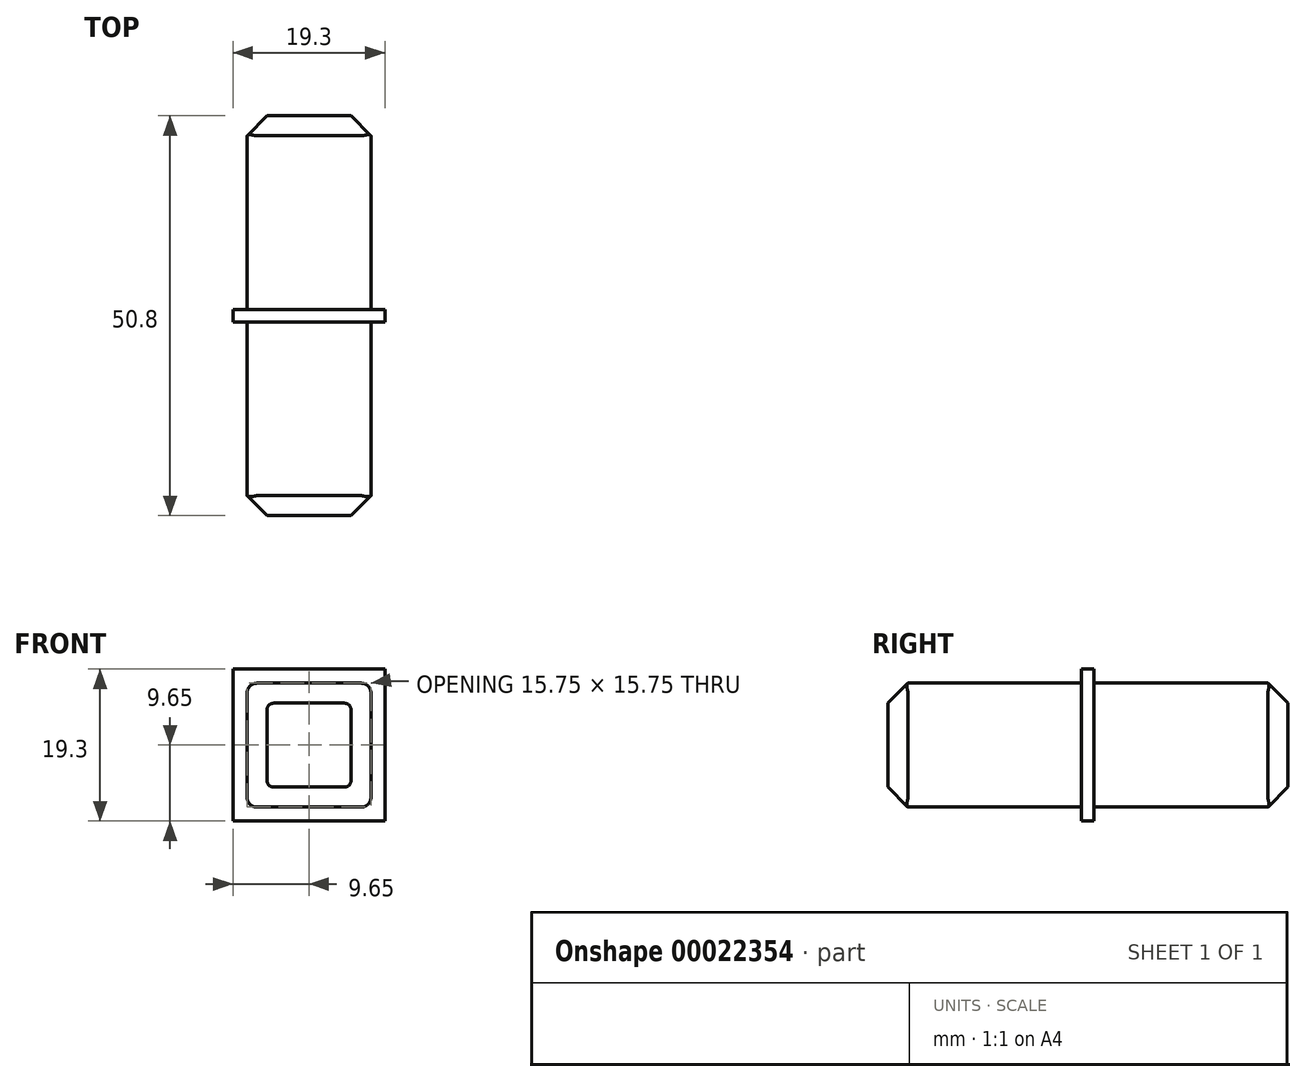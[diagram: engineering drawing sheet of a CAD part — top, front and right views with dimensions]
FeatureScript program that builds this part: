
annotation { "Feature Type Name" : "Feature", "Feature Type Description" : "" }
export const myFeature = defineFeature(function(context is Context, id is Id, definition is map)
    precondition{}
    {
        {
            var Q0;
            Q0=qCreatedBy(makeId("Front.planeOp"),FACE);
            var sketch = newSketch(context, id + "F0", { "sketchPlane" : qUnion([Q0])});
            skLineSegment(sketch, "E0.rect.bottom", {"start": v(9.65, 9.65) * mm, "end": v(-9.65, 9.65) * mm});
            skLineSegment(sketch, "E0.rect.top", {"start": v(9.65, -9.65) * mm, "end": v(-9.65, -9.65) * mm});
            skLineSegment(sketch, "E0.rect.left", {"start": v(9.65, 9.65) * mm, "end": v(9.65, -9.65) * mm});
            skLineSegment(sketch, "E0.rect.right", {"start": v(-9.65, 9.65) * mm, "end": v(-9.65, -9.65) * mm});
            skPoint(sketch, "E0.rect.middle", {"position": v(0, 0) * mm});
            skSolve(sketch);
        }
        {
            var Q0;
            Q0 = qSketchRegion(id + "F0", true);
            extrude(context, id + "F1", {"entities" : qUnion([Q0]), "endBound" : BoundingType.SYMMETRIC, "depth" : 1.59 * mm});
        }
        {
            var Q0;
            Q0=qCreatedBy(makeId("Front.planeOp"),FACE);
            var sketch = newSketch(context, id + "F2", { "sketchPlane" : qUnion([Q0])});
            skLineSegment(sketch, "E1.rect.bottom", {"start": v(7.87, 7.87) * mm, "end": v(-7.87, 7.87) * mm});
            skLineSegment(sketch, "E1.rect.top", {"start": v(7.87, -7.87) * mm, "end": v(-7.87, -7.87) * mm});
            skLineSegment(sketch, "E1.rect.left", {"start": v(7.87, 7.87) * mm, "end": v(7.87, -7.87) * mm});
            skLineSegment(sketch, "E1.rect.right", {"start": v(-7.87, 7.87) * mm, "end": v(-7.87, -7.87) * mm});
            skPoint(sketch, "E1.rect.middle", {"position": v(0, 0) * mm});
            skSolve(sketch);
        }
        {
            var Q0;
            Q0 = qSketchRegion(id + "F2", true);
            extrude(context, id + "F3", {"entities" : qUnion([Q0]), "operationType" : NewBodyOperationType.ADD, "endBound" : BoundingType.SYMMETRIC, "depth" : 50.8 * mm});
        }
        {
            var Q0;
            Q0=makeQuery(id+"F3.opExtrude","CAP_FACE",FACE,{"disambiguationData":[OSD([sQuery(id+"F2.wireOp",EDGE,"E1.rect.bottom"),sQuery(id+"F2.wireOp",EDGE,"E1.rect.top"),sQuery(id+"F2.wireOp",EDGE,"E1.rect.left"),sQuery(id+"F2.wireOp",EDGE,"E1.rect.right")])],"isStart":false});
            var Q1;
            Q1=makeQuery(id+"F3.opExtrude","CAP_FACE",FACE,{"disambiguationData":[OSD([sQuery(id+"F2.wireOp",EDGE,"E1.rect.bottom"),sQuery(id+"F2.wireOp",EDGE,"E1.rect.top"),sQuery(id+"F2.wireOp",EDGE,"E1.rect.left"),sQuery(id+"F2.wireOp",EDGE,"E1.rect.right")])],"isStart":true});
            chamfer(context, id + "F4", {"entities" : qUnion([Q0, Q1]), "width" : 2.54 * mm, "tangentPropagation" : true});
        }
        {
            var Q0;
            {var subQ0=sQuery(id+"F2.wireOp",EDGE,"E1.rect.bottom");var subQ1=sQuery(id+"F2.wireOp",EDGE,"E1.rect.left");Q0=makeQuery(id+"F3.boolean.opBoolean","SPLIT",EDGE,{"disambiguationData":[TD([makeQuery(id+"F1.opExtrude","CAP_FACE",FACE,{"disambiguationData":[OSD([sQuery(id+"F0.wireOp",EDGE,"E0.rect.bottom"),sQuery(id+"F0.wireOp",EDGE,"E0.rect.top"),sQuery(id+"F0.wireOp",EDGE,"E0.rect.left"),sQuery(id+"F0.wireOp",EDGE,"E0.rect.right")])],"isStart":false})])],"derivedFrom":makeQuery(id+"F3.opExtrude","SWEPT_EDGE",EDGE,{"disambiguationData":[OSD([subQ0,subQ1])]})});}
            var Q1;
            {var subQ0=sQuery(id+"F2.wireOp",EDGE,"E1.rect.bottom");var subQ1=sQuery(id+"F2.wireOp",EDGE,"E1.rect.right");Q1=makeQuery(id+"F3.boolean.opBoolean","SPLIT",EDGE,{"disambiguationData":[TD([makeQuery(id+"F1.opExtrude","CAP_FACE",FACE,{"disambiguationData":[OSD([sQuery(id+"F0.wireOp",EDGE,"E0.rect.bottom"),sQuery(id+"F0.wireOp",EDGE,"E0.rect.top"),sQuery(id+"F0.wireOp",EDGE,"E0.rect.left"),sQuery(id+"F0.wireOp",EDGE,"E0.rect.right")])],"isStart":false})])],"derivedFrom":makeQuery(id+"F3.opExtrude","SWEPT_EDGE",EDGE,{"disambiguationData":[OSD([subQ0,subQ1])]})});}
            var Q2;
            {var subQ0=sQuery(id+"F2.wireOp",EDGE,"E1.rect.bottom");var subQ1=sQuery(id+"F2.wireOp",EDGE,"E1.rect.left");Q2=makeQuery(id+"F3.boolean.opBoolean","SPLIT",EDGE,{"disambiguationData":[TD([makeQuery(id+"F1.opExtrude","CAP_FACE",FACE,{"disambiguationData":[OSD([sQuery(id+"F0.wireOp",EDGE,"E0.rect.bottom"),sQuery(id+"F0.wireOp",EDGE,"E0.rect.top"),sQuery(id+"F0.wireOp",EDGE,"E0.rect.left"),sQuery(id+"F0.wireOp",EDGE,"E0.rect.right")])],"isStart":true})])],"derivedFrom":makeQuery(id+"F3.opExtrude","SWEPT_EDGE",EDGE,{"disambiguationData":[OSD([subQ0,subQ1])]})});}
            var Q3;
            {var subQ0=sQuery(id+"F2.wireOp",EDGE,"E1.rect.bottom");var subQ1=sQuery(id+"F2.wireOp",EDGE,"E1.rect.right");Q3=makeQuery(id+"F3.boolean.opBoolean","SPLIT",EDGE,{"disambiguationData":[TD([makeQuery(id+"F1.opExtrude","CAP_FACE",FACE,{"disambiguationData":[OSD([sQuery(id+"F0.wireOp",EDGE,"E0.rect.bottom"),sQuery(id+"F0.wireOp",EDGE,"E0.rect.top"),sQuery(id+"F0.wireOp",EDGE,"E0.rect.left"),sQuery(id+"F0.wireOp",EDGE,"E0.rect.right")])],"isStart":true})])],"derivedFrom":makeQuery(id+"F3.opExtrude","SWEPT_EDGE",EDGE,{"disambiguationData":[OSD([subQ0,subQ1])]})});}
            var Q4;
            {var subQ0=sQuery(id+"F2.wireOp",EDGE,"E1.rect.top");var subQ1=sQuery(id+"F2.wireOp",EDGE,"E1.rect.left");Q4=makeQuery(id+"F3.boolean.opBoolean","SPLIT",EDGE,{"disambiguationData":[TD([makeQuery(id+"F1.opExtrude","CAP_FACE",FACE,{"disambiguationData":[OSD([sQuery(id+"F0.wireOp",EDGE,"E0.rect.bottom"),sQuery(id+"F0.wireOp",EDGE,"E0.rect.top"),sQuery(id+"F0.wireOp",EDGE,"E0.rect.left"),sQuery(id+"F0.wireOp",EDGE,"E0.rect.right")])],"isStart":true})])],"derivedFrom":makeQuery(id+"F3.opExtrude","SWEPT_EDGE",EDGE,{"disambiguationData":[OSD([subQ0,subQ1])]})});}
            var Q5;
            {var subQ0=sQuery(id+"F2.wireOp",EDGE,"E1.rect.top");var subQ1=sQuery(id+"F2.wireOp",EDGE,"E1.rect.right");Q5=makeQuery(id+"F3.boolean.opBoolean","SPLIT",EDGE,{"disambiguationData":[TD([makeQuery(id+"F1.opExtrude","CAP_FACE",FACE,{"disambiguationData":[OSD([sQuery(id+"F0.wireOp",EDGE,"E0.rect.bottom"),sQuery(id+"F0.wireOp",EDGE,"E0.rect.top"),sQuery(id+"F0.wireOp",EDGE,"E0.rect.left"),sQuery(id+"F0.wireOp",EDGE,"E0.rect.right")])],"isStart":true})])],"derivedFrom":makeQuery(id+"F3.opExtrude","SWEPT_EDGE",EDGE,{"disambiguationData":[OSD([subQ0,subQ1])]})});}
            var Q6;
            {var subQ0=sQuery(id+"F2.wireOp",EDGE,"E1.rect.top");var subQ1=sQuery(id+"F2.wireOp",EDGE,"E1.rect.left");Q6=makeQuery(id+"F3.boolean.opBoolean","SPLIT",EDGE,{"disambiguationData":[TD([makeQuery(id+"F1.opExtrude","CAP_FACE",FACE,{"disambiguationData":[OSD([sQuery(id+"F0.wireOp",EDGE,"E0.rect.bottom"),sQuery(id+"F0.wireOp",EDGE,"E0.rect.top"),sQuery(id+"F0.wireOp",EDGE,"E0.rect.left"),sQuery(id+"F0.wireOp",EDGE,"E0.rect.right")])],"isStart":false})])],"derivedFrom":makeQuery(id+"F3.opExtrude","SWEPT_EDGE",EDGE,{"disambiguationData":[OSD([subQ0,subQ1])]})});}
            var Q7;
            {var subQ0=sQuery(id+"F2.wireOp",EDGE,"E1.rect.top");var subQ1=sQuery(id+"F2.wireOp",EDGE,"E1.rect.right");Q7=makeQuery(id+"F3.boolean.opBoolean","SPLIT",EDGE,{"disambiguationData":[TD([makeQuery(id+"F1.opExtrude","CAP_FACE",FACE,{"disambiguationData":[OSD([sQuery(id+"F0.wireOp",EDGE,"E0.rect.bottom"),sQuery(id+"F0.wireOp",EDGE,"E0.rect.top"),sQuery(id+"F0.wireOp",EDGE,"E0.rect.left"),sQuery(id+"F0.wireOp",EDGE,"E0.rect.right")])],"isStart":false})])],"derivedFrom":makeQuery(id+"F3.opExtrude","SWEPT_EDGE",EDGE,{"disambiguationData":[OSD([subQ0,subQ1])]})});}
            var Q8;
            Q8=makeQuery(id+"F4.opChamfer","BLEND_EDGE",EDGE,{"blendedFrom":[makeQuery(id+"F3.opExtrude","CAP_EDGE",EDGE,{"disambiguationData":[OSD([sQuery(id+"F2.wireOp",EDGE,"E1.rect.top")])],"isStart":false}),makeQuery(id+"F3.opExtrude","CAP_EDGE",EDGE,{"disambiguationData":[OSD([sQuery(id+"F2.wireOp",EDGE,"E1.rect.right")])],"isStart":false})],"blendedInto":[]});
            var Q9;
            Q9=makeQuery(id+"F4.opChamfer","BLEND_EDGE",EDGE,{"blendedFrom":[makeQuery(id+"F3.opExtrude","CAP_EDGE",EDGE,{"disambiguationData":[OSD([sQuery(id+"F2.wireOp",EDGE,"E1.rect.top")])],"isStart":false}),makeQuery(id+"F3.opExtrude","CAP_EDGE",EDGE,{"disambiguationData":[OSD([sQuery(id+"F2.wireOp",EDGE,"E1.rect.left")])],"isStart":false})],"blendedInto":[]});
            var Q10;
            Q10=makeQuery(id+"F4.opChamfer","BLEND_EDGE",EDGE,{"blendedFrom":[makeQuery(id+"F3.opExtrude","CAP_EDGE",EDGE,{"disambiguationData":[OSD([sQuery(id+"F2.wireOp",EDGE,"E1.rect.bottom")])],"isStart":false}),makeQuery(id+"F3.opExtrude","CAP_EDGE",EDGE,{"disambiguationData":[OSD([sQuery(id+"F2.wireOp",EDGE,"E1.rect.left")])],"isStart":false})],"blendedInto":[]});
            var Q11;
            Q11=makeQuery(id+"F4.opChamfer","BLEND_EDGE",EDGE,{"blendedFrom":[makeQuery(id+"F3.opExtrude","CAP_EDGE",EDGE,{"disambiguationData":[OSD([sQuery(id+"F2.wireOp",EDGE,"E1.rect.bottom")])],"isStart":false}),makeQuery(id+"F3.opExtrude","CAP_EDGE",EDGE,{"disambiguationData":[OSD([sQuery(id+"F2.wireOp",EDGE,"E1.rect.right")])],"isStart":false})],"blendedInto":[]});
            var Q12;
            Q12=makeQuery(id+"F4.opChamfer","BLEND_EDGE",EDGE,{"blendedFrom":[makeQuery(id+"F3.opExtrude","CAP_EDGE",EDGE,{"disambiguationData":[OSD([sQuery(id+"F2.wireOp",EDGE,"E1.rect.top")])],"isStart":true}),makeQuery(id+"F3.opExtrude","CAP_EDGE",EDGE,{"disambiguationData":[OSD([sQuery(id+"F2.wireOp",EDGE,"E1.rect.right")])],"isStart":true})],"blendedInto":[]});
            var Q13;
            Q13=makeQuery(id+"F4.opChamfer","BLEND_EDGE",EDGE,{"blendedFrom":[makeQuery(id+"F3.opExtrude","CAP_EDGE",EDGE,{"disambiguationData":[OSD([sQuery(id+"F2.wireOp",EDGE,"E1.rect.bottom")])],"isStart":true}),makeQuery(id+"F3.opExtrude","CAP_EDGE",EDGE,{"disambiguationData":[OSD([sQuery(id+"F2.wireOp",EDGE,"E1.rect.right")])],"isStart":true})],"blendedInto":[]});
            var Q14;
            Q14=makeQuery(id+"F4.opChamfer","BLEND_EDGE",EDGE,{"blendedFrom":[makeQuery(id+"F3.opExtrude","CAP_EDGE",EDGE,{"disambiguationData":[OSD([sQuery(id+"F2.wireOp",EDGE,"E1.rect.bottom")])],"isStart":true}),makeQuery(id+"F3.opExtrude","CAP_EDGE",EDGE,{"disambiguationData":[OSD([sQuery(id+"F2.wireOp",EDGE,"E1.rect.left")])],"isStart":true})],"blendedInto":[]});
            var Q15;
            Q15=makeQuery(id+"F4.opChamfer","BLEND_EDGE",EDGE,{"blendedFrom":[makeQuery(id+"F3.opExtrude","CAP_EDGE",EDGE,{"disambiguationData":[OSD([sQuery(id+"F2.wireOp",EDGE,"E1.rect.top")])],"isStart":true}),makeQuery(id+"F3.opExtrude","CAP_EDGE",EDGE,{"disambiguationData":[OSD([sQuery(id+"F2.wireOp",EDGE,"E1.rect.left")])],"isStart":true})],"blendedInto":[]});
            fillet(context, id + "F5", {"entities" : qUnion([Q0, Q1, Q2, Q3, Q4, Q5, Q6, Q7, Q8, Q9, Q10, Q11, Q12, Q13, Q14, Q15]), "radius" : 1.27 * mm, "tangentPropagation" : true, "allowEdgeOverflow" : false});
        }
    });
